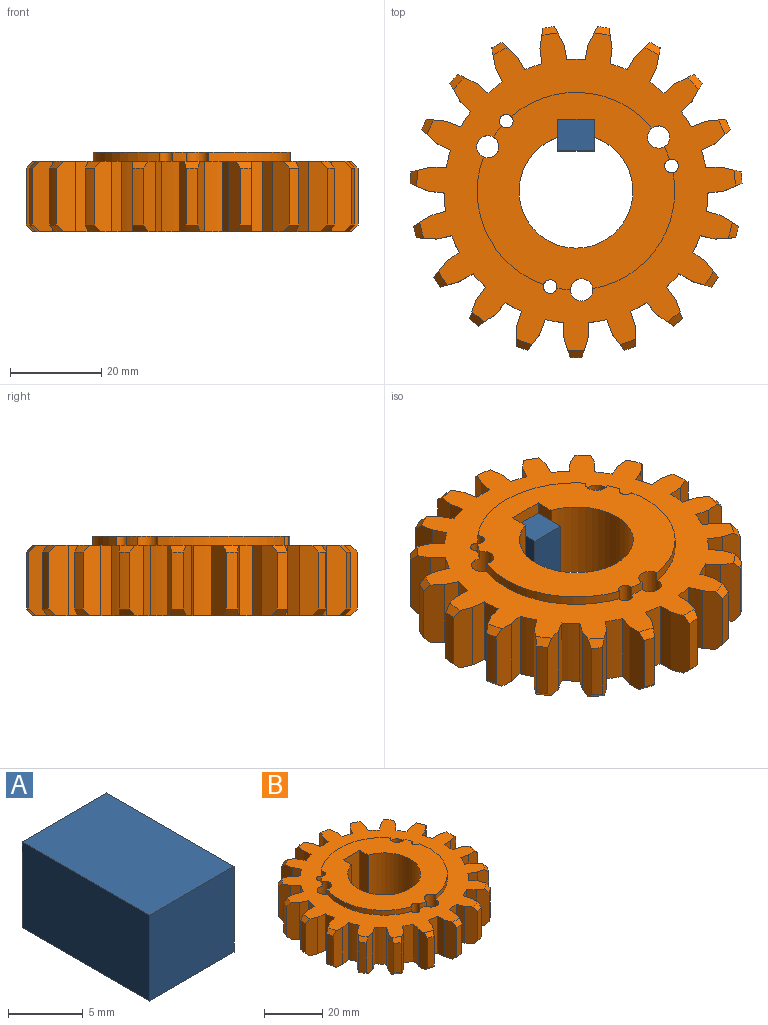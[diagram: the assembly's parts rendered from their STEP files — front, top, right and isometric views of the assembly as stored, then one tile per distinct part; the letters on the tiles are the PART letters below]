
ASSEMBLY  parts=2 mates=1
PART A: 6 faces, bbox 8x12x7 mm
  f0: plane 12x7mm, normal (-1,0,0), area 84mm2, adj f1,f3,f4,f5
  f1: plane 12x8mm, normal (0,0,-1), area 96mm2, adj f0,f2,f4,f5
  f2: plane 12x7mm, normal (1,0,0), area 84mm2, adj f1,f3,f4,f5
  f3: plane 12x8mm, normal (0,0,1), area 96mm2, adj f0,f2,f4,f5
  f4: plane 8x7mm, normal (0,-1,0), area 56mm2, adj f0,f1,f2,f3
  f5: plane 8x7mm, normal (0,1,0), area 56mm2, adj f0,f1,f2,f3
PART B: 171 faces, bbox 73x72.8x17.5 mm
  f0: cylinder r=21.7mm len=3mm, axis (0,0,-1), area 6.1mm2, adj f5,f8,f169,f170
  f1: cylinder r=21.7mm len=28.02mm, axis (0,0,-1), area 69mm2, adj f5,f8,f168,f169
  f2: cylinder r=21.7mm len=2.41mm, axis (0,0,-1), area 6.1mm2, adj f5,f8,f167,f168
  f3: cylinder r=21.7mm len=30.89mm, axis (0,0,-1), area 69mm2, adj f5,f8,f166,f167
  f4: cylinder r=21.7mm len=2.79mm, axis (0,0,-1), area 6.1mm2, adj f5,f8,f165,f166
  f5: plane 43.4x43.37mm, normal (0,0,1), area 921.9mm2, adj f0,f1,f2,f3,f4,f7,f28,f162
  f6: plane 69.96x69.77mm, normal (0,0,-1), area 2613.1mm2, adj f7,f29,f30,f31,f32,f33,f34,f35
  f7: cylinder r=12.5mm len=25mm, axis (0,0,-1), area 1231.9mm2, adj f5,f6,f162,f163
  f8: plane 69.96x69.77mm, normal (0,0,1), area 1691.1mm2, adj f0,f1,f2,f3,f4,f28,f29,f30
  f9: cylinder r=36.5mm len=12.5mm, axis (0,0,-1), area 32.1mm2, adj f116,f120,f124,f143
  f10: cylinder r=36.5mm len=12.5mm, axis (0,0,-1), area 32.1mm2, adj f111,f115,f126,f145
  f11: cylinder r=36.5mm len=12.5mm, axis (0,0,-1), area 32.1mm2, adj f106,f110,f127,f146
  f12: cylinder r=36.5mm len=12.5mm, axis (0,0,-1), area 32.1mm2, adj f101,f105,f128,f147
  f13: cylinder r=36.5mm len=12.5mm, axis (0,0,-1), area 32.1mm2, adj f96,f100,f129,f148
  f14: cylinder r=36.5mm len=12.5mm, axis (0,0,-1), area 32.1mm2, adj f91,f95,f130,f149
  f15: cylinder r=36.5mm len=12.5mm, axis (0,0,-1), area 32.1mm2, adj f86,f90,f131,f150
  f16: cylinder r=36.5mm len=12.5mm, axis (0,0,-1), area 32.1mm2, adj f81,f85,f132,f151
  f17: cylinder r=36.5mm len=12.5mm, axis (0,0,-1), area 32.1mm2, adj f76,f80,f133,f152
  f18: cylinder r=36.5mm len=12.5mm, axis (0,0,-1), area 32.1mm2, adj f71,f75,f134,f153
  f19: cylinder r=36.5mm len=12.5mm, axis (0,0,-1), area 32.1mm2, adj f66,f70,f135,f154
  f20: cylinder r=36.5mm len=12.5mm, axis (0,0,-1), area 32.1mm2, adj f61,f65,f136,f155
  f21: cylinder r=36.5mm len=12.5mm, axis (0,0,-1), area 32.1mm2, adj f56,f60,f137,f156
  f22: cylinder r=36.5mm len=12.5mm, axis (0,0,-1), area 32.1mm2, adj f51,f55,f138,f157
  f23: cylinder r=36.5mm len=12.5mm, axis (0,0,-1), area 32.1mm2, adj f46,f50,f139,f158
  f24: cylinder r=36.5mm len=12.5mm, axis (0,0,-1), area 32.1mm2, adj f41,f45,f140,f159
  f25: cylinder r=36.5mm len=12.5mm, axis (0,0,-1), area 32.1mm2, adj f36,f40,f141,f160
  f26: cylinder r=36.5mm len=12.5mm, axis (0,0,-1), area 32.1mm2, adj f31,f35,f142,f161
  f27: cylinder r=36.5mm len=12.5mm, axis (0,0,-1), area 32.1mm2, adj f30,f121,f125,f144
  f28: cylinder r=21.7mm len=25.48mm, axis (0,0,-1), area 69mm2, adj f5,f8,f165,f170
  f29: plane 15.5x3.3mm, normal (-0.98,0.2,0), area 52.2mm2, adj f6,f8,f30,f33
  f30: plane 15.51x4mm, normal (-0.89,0.46,0), area 67.3mm2, adj f6,f8,f27,f29,f125,f144
  f31: plane 15.51x4mm, normal (0.89,0.46,0), area 67.3mm2, adj f6,f8,f26,f32,f142,f161
  f32: plane 15.5x3.3mm, normal (0.98,0.2,0), area 52.2mm2, adj f6,f8,f31,f33
  f33: cylinder r=28.97mm len=15.5mm, axis (0,0,1), area 62mm2, adj f6,f8,f29,f32
  f34: plane 15.5x3.34mm, normal (-0.99,-0.13,0), area 52.2mm2, adj f6,f8,f35,f38
  f35: plane 15.51x4.46mm, normal (-0.99,0.15,0), area 67.3mm2, adj f6,f8,f26,f34,f142,f161
  f36: plane 15.51x3.27mm, normal (0.69,0.72,0), area 67.3mm2, adj f6,f8,f25,f37,f141,f160
  f37: plane 15.5x2.9mm, normal (0.86,0.51,0), area 52.2mm2, adj f6,f8,f36,f38
  f38: cylinder r=28.97mm len=15.5mm, axis (0,0,1), area 62mm2, adj f6,f8,f34,f37
  f39: plane 15.5x3.01mm, normal (-0.9,-0.45,0), area 52.2mm2, adj f6,f8,f40,f43
  f40: plane 15.51x4.43mm, normal (-0.98,-0.18,0), area 67.3mm2, adj f6,f8,f25,f39,f141,f160
  f41: plane 15.51x4.1mm, normal (0.42,0.91,0), area 67.3mm2, adj f6,f8,f24,f42,f140,f159
  f42: plane 15.5x2.55mm, normal (0.65,0.76,0), area 52.2mm2, adj f6,f8,f41,f43
  f43: cylinder r=28.97mm len=15.5mm, axis (0,0,1), area 62mm2, adj f6,f8,f39,f42
  f44: plane 15.5x2.4mm, normal (-0.7,-0.71,0), area 52.2mm2, adj f6,f8,f45,f48
  f45: plane 15.51x3.93mm, normal (-0.87,-0.49,0), area 67.3mm2, adj f6,f8,f24,f44,f140,f159
  f46: plane 15.51x4.49mm, normal (0.1,1,0), area 67.3mm2, adj f6,f8,f23,f47,f139,f158
  f47: plane 15.5x3.13mm, normal (0.37,0.93,0), area 52.2mm2, adj f6,f8,f46,f48
  f48: cylinder r=28.97mm len=15.5mm, axis (0,0,1), area 62mm2, adj f6,f8,f44,f47
  f49: plane 15.5x3.04mm, normal (-0.43,-0.9,0), area 52.2mm2, adj f6,f8,f50,f53
  f50: plane 15.51x3.37mm, normal (-0.66,-0.75,0), area 67.3mm2, adj f6,f8,f23,f49,f139,f158
  f51: plane 15.51x4.39mm, normal (-0.23,0.97,0), area 67.3mm2, adj f6,f8,f22,f52,f138,f157
  f52: plane 15.5x3.36mm, normal (0.05,1,0), area 52.2mm2, adj f6,f8,f51,f53
  f53: cylinder r=28.97mm len=15.5mm, axis (0,0,1), area 62mm2, adj f6,f8,f49,f52
  f54: plane 15.5x3.34mm, normal (-0.12,-0.99,0), area 52.2mm2, adj f6,f8,f55,f58
  f55: plane 15.51x4.16mm, normal (-0.39,-0.92,0), area 67.3mm2, adj f6,f8,f22,f54,f138,f157
  f56: plane 15.51x3.82mm, normal (-0.53,0.85,0), area 67.3mm2, adj f6,f8,f21,f57,f137,f156
  f57: plane 15.5x3.23mm, normal (-0.28,0.96,0), area 52.2mm2, adj f6,f8,f56,f58
  f58: cylinder r=28.97mm len=15.5mm, axis (0,0,1), area 62mm2, adj f6,f8,f54,f57
  f59: plane 15.5x3.29mm, normal (0.21,-0.98,0), area 52.2mm2, adj f6,f8,f60,f63
  f60: plane 15.51x4.5mm, normal (-0.07,-1,0), area 67.3mm2, adj f6,f8,f21,f59,f137,f156
  f61: plane 15.51x3.51mm, normal (-0.78,0.63,0), area 67.3mm2, adj f6,f8,f20,f62,f136,f155
  f62: plane 15.5x2.75mm, normal (-0.58,0.82,0), area 52.2mm2, adj f6,f8,f61,f63
  f63: cylinder r=28.97mm len=15.5mm, axis (0,0,1), area 62mm2, adj f6,f8,f59,f62
  f64: plane 15.5x2.88mm, normal (0.52,-0.86,0), area 52.2mm2, adj f6,f8,f65,f68
  f65: plane 15.51x4.35mm, normal (0.26,-0.97,0), area 67.3mm2, adj f6,f8,f20,f64,f136,f155
  f66: plane 15.51x4.24mm, normal (-0.94,0.34,0), area 67.3mm2, adj f6,f8,f19,f67,f135,f154
  f67: plane 15.5x2.73mm, normal (-0.81,0.59,0), area 52.2mm2, adj f6,f8,f66,f68
  f68: cylinder r=28.97mm len=15.5mm, axis (0,0,1), area 62mm2, adj f6,f8,f64,f67
  f69: plane 15.5x2.58mm, normal (0.77,-0.64,0), area 52.2mm2, adj f6,f8,f70,f73
  f70: plane 15.51x3.73mm, normal (0.56,-0.83,0), area 67.3mm2, adj f6,f8,f19,f69,f135,f154
  f71: plane 15.51x4.51mm, normal (-1,0.02,0), area 67.3mm2, adj f6,f8,f18,f72,f134,f153
  f72: plane 15.5x3.22mm, normal (-0.96,0.29,0), area 52.2mm2, adj f6,f8,f71,f73
  f73: cylinder r=28.97mm len=15.5mm, axis (0,0,1), area 62mm2, adj f6,f8,f69,f72
  f74: plane 15.5x3.15mm, normal (0.93,-0.36,0), area 52.2mm2, adj f6,f8,f75,f78
  f75: plane 15.51x3.61mm, normal (0.8,-0.6,0), area 67.3mm2, adj f6,f8,f18,f74,f134,f153
  f76: plane 15.51x4.29mm, normal (-0.95,-0.31,0), area 67.3mm2, adj f6,f8,f17,f77,f133,f152
  f77: plane 15.5x3.37mm, normal (-1,-0.03,0), area 52.2mm2, adj f6,f8,f76,f78
  f78: cylinder r=28.97mm len=15.5mm, axis (0,0,1), area 62mm2, adj f6,f8,f74,f77
  f79: plane 15.5x3.37mm, normal (1,-0.03,0), area 52.2mm2, adj f6,f8,f80,f83
  f80: plane 15.51x4.29mm, normal (0.95,-0.31,0), area 67.3mm2, adj f6,f8,f17,f79,f133,f152
  f81: plane 15.51x3.61mm, normal (-0.8,-0.6,0), area 67.3mm2, adj f6,f8,f16,f82,f132,f151
  f82: plane 15.5x3.15mm, normal (-0.93,-0.36,0), area 52.2mm2, adj f6,f8,f81,f83
  f83: cylinder r=28.97mm len=15.5mm, axis (0,0,1), area 62mm2, adj f6,f8,f79,f82
  f84: plane 15.5x3.22mm, normal (0.96,0.29,0), area 52.2mm2, adj f6,f8,f85,f88
  f85: plane 15.51x4.51mm, normal (1,0.02,0), area 67.3mm2, adj f6,f8,f16,f84,f132,f151
  f86: plane 15.51x3.73mm, normal (-0.56,-0.83,0), area 67.3mm2, adj f6,f8,f15,f87,f131,f150
  f87: plane 15.5x2.58mm, normal (-0.77,-0.64,0), area 52.2mm2, adj f6,f8,f86,f88
  f88: cylinder r=28.97mm len=15.5mm, axis (0,0,1), area 62mm2, adj f6,f8,f84,f87
  f89: plane 15.5x2.73mm, normal (0.81,0.59,0), area 52.2mm2, adj f6,f8,f90,f93
  f90: plane 15.51x4.24mm, normal (0.94,0.34,0), area 67.3mm2, adj f6,f8,f15,f89,f131,f150
  f91: plane 15.51x4.35mm, normal (-0.26,-0.97,0), area 67.3mm2, adj f6,f8,f14,f92,f130,f149
  f92: plane 15.5x2.88mm, normal (-0.52,-0.86,0), area 52.2mm2, adj f6,f8,f91,f93
  f93: cylinder r=28.97mm len=15.5mm, axis (0,0,1), area 62mm2, adj f6,f8,f89,f92
  f94: plane 15.5x2.75mm, normal (0.58,0.82,0), area 52.2mm2, adj f6,f8,f95,f98
  f95: plane 15.51x3.51mm, normal (0.78,0.63,0), area 67.3mm2, adj f6,f8,f14,f94,f130,f149
  f96: plane 15.51x4.5mm, normal (0.07,-1,0), area 67.3mm2, adj f6,f8,f13,f97,f129,f148
  f97: plane 15.5x3.29mm, normal (-0.21,-0.98,0), area 52.2mm2, adj f6,f8,f96,f98
  f98: cylinder r=28.97mm len=15.5mm, axis (0,0,1), area 62mm2, adj f6,f8,f94,f97
  f99: plane 15.5x3.23mm, normal (0.28,0.96,0), area 52.2mm2, adj f6,f8,f100,f103
  f100: plane 15.51x3.82mm, normal (0.53,0.85,0), area 67.3mm2, adj f6,f8,f13,f99,f129,f148
  f101: plane 15.51x4.16mm, normal (0.39,-0.92,0), area 67.3mm2, adj f6,f8,f12,f102,f128,f147
  f102: plane 15.5x3.34mm, normal (0.12,-0.99,0), area 52.2mm2, adj f6,f8,f101,f103
  f103: cylinder r=28.97mm len=15.5mm, axis (0,0,1), area 62mm2, adj f6,f8,f99,f102
  f104: plane 15.5x3.36mm, normal (-0.05,1,0), area 52.2mm2, adj f6,f8,f105,f108
  f105: plane 15.51x4.39mm, normal (0.23,0.97,0), area 67.3mm2, adj f6,f8,f12,f104,f128,f147
  f106: plane 15.51x3.37mm, normal (0.66,-0.75,0), area 67.3mm2, adj f6,f8,f11,f107,f127,f146
  f107: plane 15.5x3.04mm, normal (0.43,-0.9,0), area 52.2mm2, adj f6,f8,f106,f108
  f108: cylinder r=28.97mm len=15.5mm, axis (0,0,1), area 62mm2, adj f6,f8,f104,f107
  f109: plane 15.5x3.13mm, normal (-0.37,0.93,0), area 52.2mm2, adj f6,f8,f110,f113
  f110: plane 15.51x4.49mm, normal (-0.1,1,0), area 67.3mm2, adj f6,f8,f11,f109,f127,f146
  f111: plane 15.51x3.93mm, normal (0.87,-0.49,0), area 67.3mm2, adj f6,f8,f10,f112,f126,f145
  f112: plane 15.5x2.4mm, normal (0.7,-0.71,0), area 52.2mm2, adj f6,f8,f111,f113
  f113: cylinder r=28.97mm len=15.5mm, axis (0,0,1), area 62mm2, adj f6,f8,f109,f112
  f114: plane 15.5x2.55mm, normal (-0.65,0.76,0), area 52.2mm2, adj f6,f8,f115,f118
  f115: plane 15.51x4.1mm, normal (-0.42,0.91,0), area 67.3mm2, adj f6,f8,f10,f114,f126,f145
  f116: plane 15.51x4.43mm, normal (0.98,-0.18,0), area 67.3mm2, adj f6,f8,f9,f117,f124,f143
  f117: plane 15.5x3.01mm, normal (0.9,-0.45,0), area 52.2mm2, adj f6,f8,f116,f118
  f118: cylinder r=28.97mm len=15.5mm, axis (0,0,1), area 62mm2, adj f6,f8,f114,f117
  f119: plane 15.5x2.9mm, normal (-0.86,0.51,0), area 52.2mm2, adj f6,f8,f120,f123
  f120: plane 15.51x3.27mm, normal (-0.69,0.72,0), area 67.3mm2, adj f6,f8,f9,f119,f124,f143
  f121: plane 15.51x4.46mm, normal (0.99,0.15,0), area 67.3mm2, adj f6,f8,f27,f122,f125,f144
  f122: plane 15.5x3.34mm, normal (0.99,-0.13,0), area 52.2mm2, adj f6,f8,f121,f123
  f123: cylinder r=28.97mm len=15.5mm, axis (0,0,1), area 62mm2, adj f6,f8,f119,f122
  f124: cone r=36.5mm half-angle=45deg, axis (0,0,-1), area 6.5mm2, adj f8,f9,f116,f120
  f125: cone r=36.5mm half-angle=45deg, axis (0,0,-1), area 6.5mm2, adj f8,f27,f30,f121
  f126: cone r=36.5mm half-angle=45deg, axis (0,0,-1), area 6.5mm2, adj f8,f10,f111,f115
  f127: cone r=36.5mm half-angle=45deg, axis (0,0,-1), area 6.5mm2, adj f8,f11,f106,f110
  f128: cone r=36.5mm half-angle=45deg, axis (0,0,-1), area 6.5mm2, adj f8,f12,f101,f105
  f129: cone r=36.5mm half-angle=45deg, axis (0,0,-1), area 6.5mm2, adj f8,f13,f96,f100
  f130: cone r=36.5mm half-angle=45deg, axis (0,0,-1), area 6.5mm2, adj f8,f14,f91,f95
  f131: cone r=36.5mm half-angle=45deg, axis (0,0,-1), area 6.5mm2, adj f8,f15,f86,f90
  f132: cone r=36.5mm half-angle=45deg, axis (0,0,-1), area 6.5mm2, adj f8,f16,f81,f85
  f133: cone r=36.5mm half-angle=45deg, axis (0,0,-1), area 6.5mm2, adj f8,f17,f76,f80
  f134: cone r=36.5mm half-angle=45deg, axis (0,0,-1), area 6.5mm2, adj f8,f18,f71,f75
  f135: cone r=36.5mm half-angle=45deg, axis (0,0,-1), area 6.5mm2, adj f8,f19,f66,f70
  f136: cone r=36.5mm half-angle=45deg, axis (0,0,-1), area 6.5mm2, adj f8,f20,f61,f65
  f137: cone r=36.5mm half-angle=45deg, axis (0,0,-1), area 6.5mm2, adj f8,f21,f56,f60
  f138: cone r=36.5mm half-angle=45deg, axis (0,0,-1), area 6.5mm2, adj f8,f22,f51,f55
  f139: cone r=36.5mm half-angle=45deg, axis (0,0,-1), area 6.5mm2, adj f8,f23,f46,f50
  f140: cone r=36.5mm half-angle=45deg, axis (0,0,-1), area 6.5mm2, adj f8,f24,f41,f45
  f141: cone r=36.5mm half-angle=45deg, axis (0,0,-1), area 6.5mm2, adj f8,f25,f36,f40
  f142: cone r=36.5mm half-angle=45deg, axis (0,0,-1), area 6.5mm2, adj f8,f26,f31,f35
  f143: cone r=35mm half-angle=45deg, axis (0,0,1), area 6.5mm2, adj f6,f9,f116,f120
  f144: cone r=35mm half-angle=45deg, axis (0,0,1), area 6.5mm2, adj f6,f27,f30,f121
  f145: cone r=35mm half-angle=45deg, axis (0,0,1), area 6.5mm2, adj f6,f10,f111,f115
  f146: cone r=35mm half-angle=45deg, axis (0,0,1), area 6.5mm2, adj f6,f11,f106,f110
  f147: cone r=35mm half-angle=45deg, axis (0,0,1), area 6.5mm2, adj f6,f12,f101,f105
  f148: cone r=35mm half-angle=45deg, axis (0,0,1), area 6.5mm2, adj f6,f13,f96,f100
  f149: cone r=35mm half-angle=45deg, axis (0,0,1), area 6.5mm2, adj f6,f14,f91,f95
  f150: cone r=35mm half-angle=45deg, axis (0,0,1), area 6.5mm2, adj f6,f15,f86,f90
  f151: cone r=35mm half-angle=45deg, axis (0,0,1), area 6.5mm2, adj f6,f16,f81,f85
  f152: cone r=35mm half-angle=45deg, axis (0,0,1), area 6.5mm2, adj f6,f17,f76,f80
  f153: cone r=35mm half-angle=45deg, axis (0,0,1), area 6.5mm2, adj f6,f18,f71,f75
  f154: cone r=35mm half-angle=45deg, axis (0,0,1), area 6.5mm2, adj f6,f19,f66,f70
  f155: cone r=35mm half-angle=45deg, axis (0,0,1), area 6.5mm2, adj f6,f20,f61,f65
  f156: cone r=35mm half-angle=45deg, axis (0,0,1), area 6.5mm2, adj f6,f21,f56,f60
  f157: cone r=35mm half-angle=45deg, axis (0,0,1), area 6.5mm2, adj f6,f22,f51,f55
  f158: cone r=35mm half-angle=45deg, axis (0,0,1), area 6.5mm2, adj f6,f23,f46,f50
  f159: cone r=35mm half-angle=45deg, axis (0,0,1), area 6.5mm2, adj f6,f24,f41,f45
  f160: cone r=35mm half-angle=45deg, axis (0,0,1), area 6.5mm2, adj f6,f25,f36,f40
  f161: cone r=35mm half-angle=45deg, axis (0,0,1), area 6.5mm2, adj f6,f26,f31,f35
  f162: plane 17.5x4mm, normal (1,0,0), area 70mm2, adj f5,f6,f7,f164
  f163: plane 17.5x4mm, normal (-1,0,0), area 70mm2, adj f5,f6,f7,f164
  f164: plane 17.5x8mm, normal (0,-1,0), area 140mm2, adj f5,f6,f162,f163
  f165: cylinder r=1.5mm len=17.5mm, axis (0,0,1), area 155.3mm2, adj f4,f5,f6,f8,f28
  f166: cylinder r=2.45mm len=17.5mm, axis (0,0,1), area 253.4mm2, adj f3,f4,f5,f6,f8
  f167: cylinder r=1.5mm len=17.5mm, axis (0,0,1), area 155.3mm2, adj f2,f3,f5,f6,f8
  f168: cylinder r=2.45mm len=17.5mm, axis (0,0,1), area 253.4mm2, adj f1,f2,f5,f6,f8
  f169: cylinder r=1.5mm len=17.5mm, axis (0,0,1), area 155.3mm2, adj f0,f1,f5,f6,f8
  f170: cylinder r=2.45mm len=17.5mm, axis (0,0,1), area 253.4mm2, adj f0,f5,f6,f8,f28
PLACE A rot(axis=(-1,0,0),90deg) t=(31.21,13.96,-29.06)mm
PLACE B t=(35.21,5.11,-31.81)mm
MATE fastened A.f3 <-> B.f164  axis (0,1,0) through (35.21,20.96,-23.06)mm
